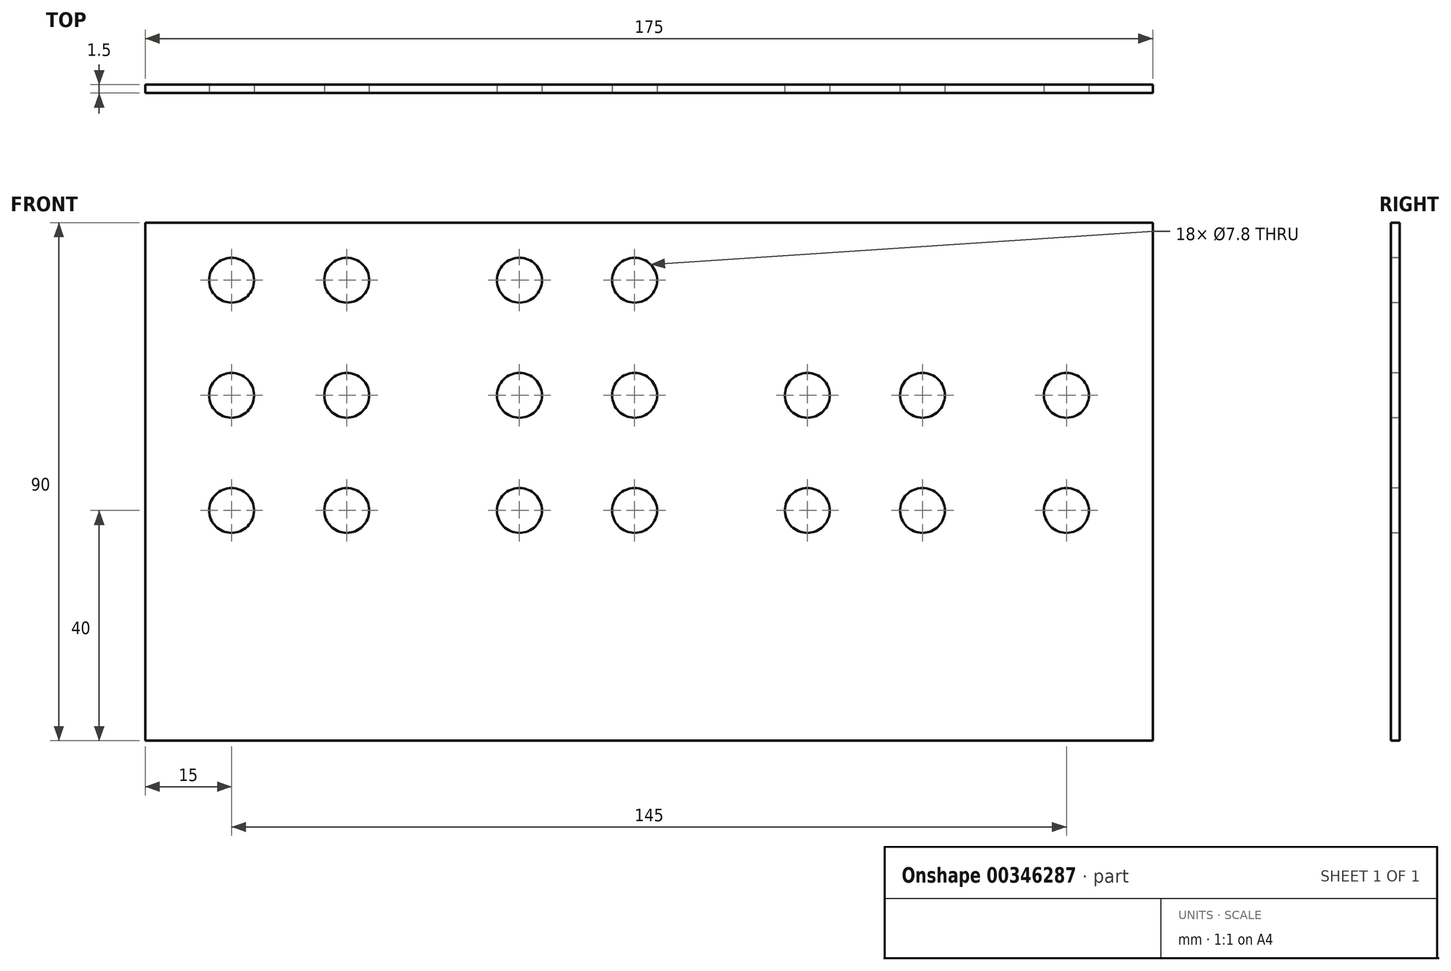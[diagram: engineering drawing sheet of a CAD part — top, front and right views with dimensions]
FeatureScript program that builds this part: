
annotation { "Feature Type Name" : "Feature", "Feature Type Description" : "" }
export const myFeature = defineFeature(function(context is Context, id is Id, definition is map)
    precondition{}
    {
        {
            var Q0;
            Q0=qCreatedBy(makeId("Front.planeOp"),FACE);
            var sketch = newSketch(context, id + "F0", { "sketchPlane" : qUnion([Q0])});
            skLineSegment(sketch, "E0.bottom", {"start": v(-87.5, -45) * mm, "end": v(87.5, -45) * mm});
            skLineSegment(sketch, "E0.top", {"start": v(-87.5, 45) * mm, "end": v(87.5, 45) * mm});
            skLineSegment(sketch, "E0.left", {"start": v(-87.5, -45) * mm, "end": v(-87.5, 45) * mm});
            skLineSegment(sketch, "E0.right", {"start": v(87.5, -45) * mm, "end": v(87.5, 45) * mm});
            skPoint(sketch, "E0.middle", {"position": v(0, 0) * mm});
            skPoint(sketch, "E1", {"position": v(72.5, -5) * mm});
            skPoint(sketch, "E2", {"position": v(72.5, 15) * mm});
            skPoint(sketch, "E3", {"position": v(47.5, 15) * mm});
            skPoint(sketch, "E4", {"position": v(47.5, -5) * mm});
            skPoint(sketch, "E5", {"position": v(27.5, -5) * mm});
            skPoint(sketch, "E6", {"position": v(27.5, 15) * mm});
            skCircle(sketch, "E7", {"center": v(72.5, -5) * mm, "radius": 3.9 * mm});
            skCircle(sketch, "E8", {"center": v(47.5, -5) * mm, "radius": 3.9 * mm});
            skCircle(sketch, "E9", {"center": v(27.5, -5) * mm, "radius": 3.9 * mm});
            skCircle(sketch, "E10", {"center": v(27.5, 15) * mm, "radius": 3.9 * mm});
            skCircle(sketch, "E11", {"center": v(47.5, 15) * mm, "radius": 3.9 * mm});
            skCircle(sketch, "E12", {"center": v(72.5, 15) * mm, "radius": 3.9 * mm});
            skPoint(sketch, "E13", {"position": v(-72.5, -5) * mm});
            skPoint(sketch, "E14", {"position": v(-52.5, -5) * mm});
            skPoint(sketch, "E15", {"position": v(-22.5, -5) * mm});
            skPoint(sketch, "E16", {"position": v(-2.5, -5) * mm});
            skPoint(sketch, "E17", {"position": v(-2.5, 15) * mm});
            skPoint(sketch, "E18", {"position": v(-22.5, 15) * mm});
            skPoint(sketch, "E19", {"position": v(-52.5, 15) * mm});
            skPoint(sketch, "E20", {"position": v(-72.5, 15) * mm});
            skPoint(sketch, "E21", {"position": v(-2.5, 35) * mm});
            skPoint(sketch, "E22", {"position": v(-22.5, 35) * mm});
            skPoint(sketch, "E23", {"position": v(-52.5, 35) * mm});
            skPoint(sketch, "E24", {"position": v(-72.5, 35) * mm});
            skCircle(sketch, "E25", {"center": v(-2.5, -5) * mm, "radius": 3.9 * mm});
            skCircle(sketch, "E26", {"center": v(-2.5, 15) * mm, "radius": 3.9 * mm});
            skCircle(sketch, "E27", {"center": v(-2.5, 35) * mm, "radius": 3.9 * mm});
            skCircle(sketch, "E28", {"center": v(-22.5, 35) * mm, "radius": 3.9 * mm});
            skCircle(sketch, "E29", {"center": v(-22.5, 15) * mm, "radius": 3.9 * mm});
            skCircle(sketch, "E30", {"center": v(-22.5, -5) * mm, "radius": 3.9 * mm});
            skCircle(sketch, "E31", {"center": v(-52.5, -5) * mm, "radius": 3.9 * mm});
            skCircle(sketch, "E32", {"center": v(-52.5, 15) * mm, "radius": 3.9 * mm});
            skCircle(sketch, "E33", {"center": v(-52.5, 35) * mm, "radius": 3.9 * mm});
            skCircle(sketch, "E34", {"center": v(-72.5, 15) * mm, "radius": 3.9 * mm});
            skCircle(sketch, "E35", {"center": v(-72.5, 35) * mm, "radius": 3.9 * mm});
            skCircle(sketch, "E36", {"center": v(-72.5, -5) * mm, "radius": 3.9 * mm});
            skSolve(sketch);
        }
        {
            var Q0;
            Q0=makeQuery(id+"F0.imprint","IMPRINT",FACE,{"disambiguationData":[TD([[makeQuery(id+"F0.imprint","IMPRINT",EDGE,{"derivedFrom":sQuery(id+"F0.wireOp",EDGE,"E0.bottom")}),1.0]])]});
            extrude(context, id + "F1", {"entities" : qUnion([Q0]), "oppositeDirection" : true, "depth" : 1.5 * mm});
        }
    });
